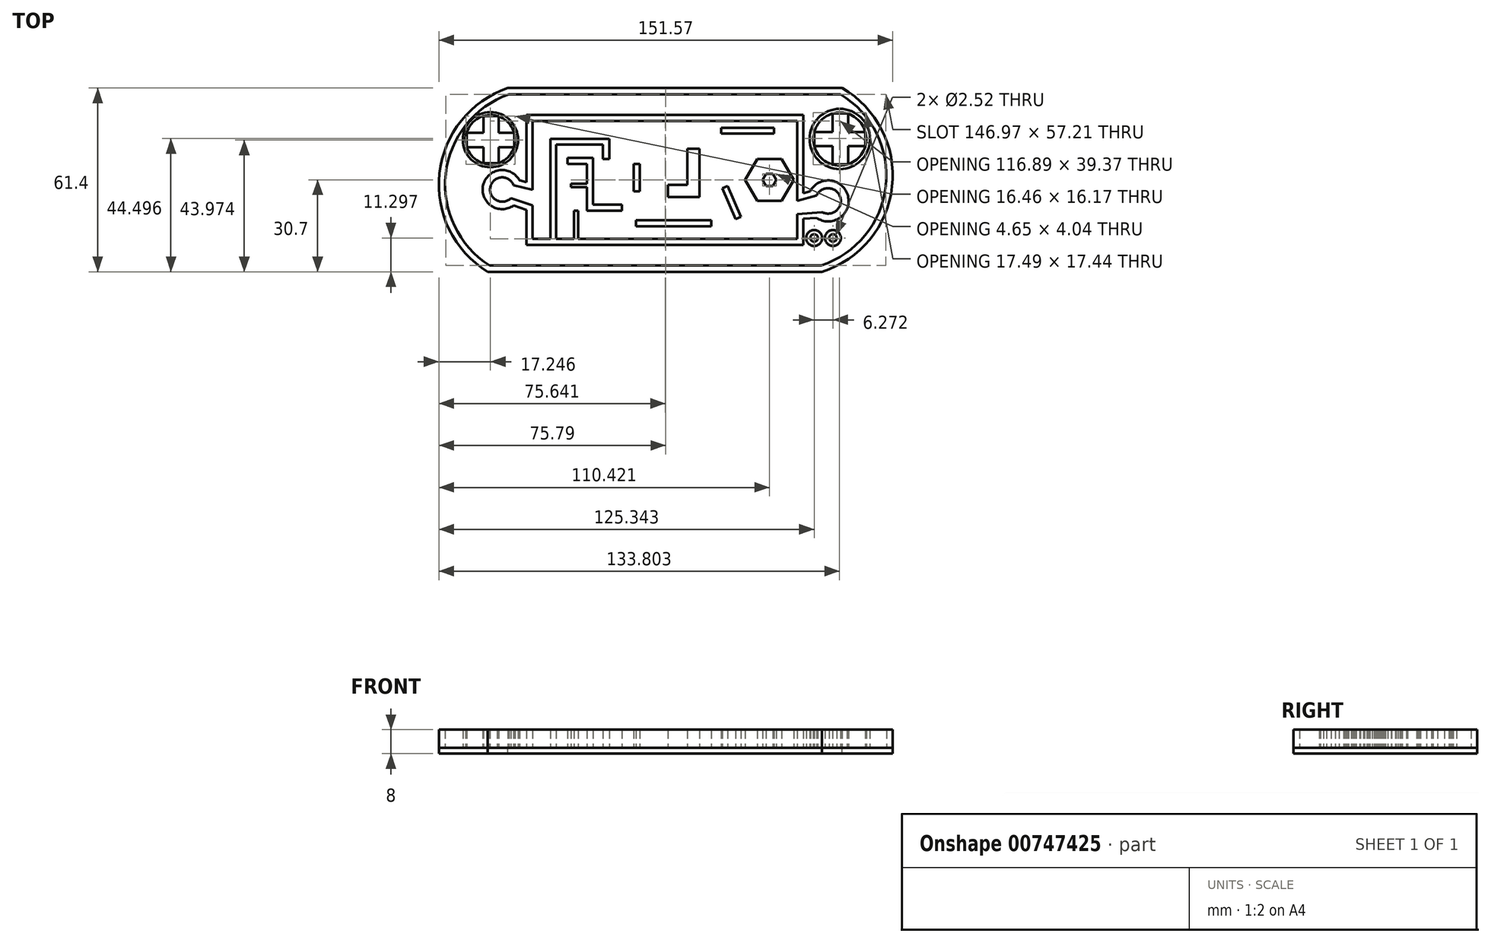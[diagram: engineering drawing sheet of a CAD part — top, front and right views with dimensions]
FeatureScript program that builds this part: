
annotation { "Feature Type Name" : "Feature", "Feature Type Description" : "" }
export const myFeature = defineFeature(function(context is Context, id is Id, definition is map)
    precondition{}
    {
        {
            var Q0;
            Q0=qCreatedBy(makeId("Top.planeOp"),FACE);
            var sketch = newSketch(context, id + "F0", { "sketchPlane" : qUnion([Q0])});
            skLineSegment(sketch, "E0.bottom", {"start": v(-52.45, 30.7) * mm, "end": v(59.2, 30.7) * mm});
            skLineSegment(sketch, "E0.top", {"start": v(-59.2, -30.7) * mm, "end": v(52.45, -30.7) * mm});
            skPoint(sketch, "E0.middle", {"position": v(0, 0) * mm});
            skArc(sketch, "E1", {"start": v(-52.45, 30.7) * mm, "mid": v(-75.31, 2.14) * mm, "end": v(-59.2, -30.7) * mm});
            skArc(sketch, "E2", {"start": v(52.45, -30.7) * mm, "mid": v(75.85, -2.2) * mm, "end": v(59.2, 30.7) * mm});
            skLineSegment(sketch, "E3.bottom", {"start": v(-46.23, 21.68) * mm, "end": v(46.23, 21.68) * mm});
            skLineSegment(sketch, "E3.top", {"start": v(-46.23, -21.68) * mm, "end": v(46.23, -21.68) * mm});
            skLineSegment(sketch, "E3.left", {"start": v(-46.23, 21.68) * mm, "end": v(-46.23, -0.76) * mm});
            skLineSegment(sketch, "E3.right", {"start": v(46.23, 21.68) * mm, "end": v(46.23, -4.42) * mm});
            skCircle(sketch, "E4", {"center": v(-58.27, 13.42) * mm, "radius": 8.27 * mm});
            skLineSegment(sketch, "E5.bottom", {"start": v(-60.57, 21.36) * mm, "end": v(-55.57, 21.36) * mm});
            skLineSegment(sketch, "E5.top", {"start": v(-60.57, 5.6) * mm, "end": v(-55.57, 5.6) * mm});
            skLineSegment(sketch, "E5.left", {"start": v(-60.57, 21.36) * mm, "end": v(-60.57, 15.78) * mm});
            skLineSegment(sketch, "E5.right", {"start": v(-55.57, 21.36) * mm, "end": v(-55.57, 15.78) * mm});
            skLineSegment(sketch, "E6.bottom", {"start": v(-66.16, 10.93) * mm, "end": v(-60.57, 10.93) * mm});
            skLineSegment(sketch, "E6.top", {"start": v(-66.16, 15.78) * mm, "end": v(-60.57, 15.78) * mm});
            skLineSegment(sketch, "E6.left", {"start": v(-66.16, 10.93) * mm, "end": v(-66.16, 15.78) * mm});
            skLineSegment(sketch, "E6.right", {"start": v(-50.36, 10.93) * mm, "end": v(-50.36, 15.78) * mm});
            skLineSegment(sketch, "E7", {"start": v(-55.57, 15.78) * mm, "end": v(-58.27, 13.42) * mm});
            skLineSegment(sketch, "E8", {"start": v(-55.57, 10.93) * mm, "end": v(-58.27, 13.42) * mm});
            skLineSegment(sketch, "E9", {"start": v(-58.27, 13.42) * mm, "end": v(-60.57, 10.93) * mm});
            skLineSegment(sketch, "E10", {"start": v(-58.27, 13.42) * mm, "end": v(-60.57, 15.78) * mm});
            skLineSegment(sketch, "E11.trimOffspring", {"start": v(-55.57, 10.93) * mm, "end": v(-55.57, 5.6) * mm});
            skLineSegment(sketch, "E12.trimOffspring", {"start": v(-55.57, 15.78) * mm, "end": v(-50.36, 15.78) * mm});
            skLineSegment(sketch, "E13.trimOffspring", {"start": v(-60.57, 10.93) * mm, "end": v(-60.57, 5.6) * mm});
            skLineSegment(sketch, "E14.trimOffspring", {"start": v(-55.57, 10.93) * mm, "end": v(-50.36, 10.93) * mm});
            skArc(sketch, "E15", {"start": v(-48.56, -0.18) * mm, "mid": v(-60.71, -1.71) * mm, "end": v(-50.56, -8.57) * mm});
            skPoint(sketch, "E16.start.orphan", {"position": v(-60.98, 5.6) * mm});
            skArc(sketch, "E17", {"start": v(-50.57, -1.75) * mm, "mid": v(-58.32, -2.38) * mm, "end": v(-51.51, -6.14) * mm});
            skCircle(sketch, "E18", {"center": v(58.4, 13.66) * mm, "radius": 8.85 * mm});
            skArc(sketch, "E19", {"start": v(50.6, -12.67) * mm, "mid": v(61.14, -5.42) * mm, "end": v(48.46, -3.79) * mm});
            skArc(sketch, "E20", {"start": v(52.48, -10.76) * mm, "mid": v(58.52, -5.71) * mm, "end": v(50.67, -5.19) * mm});
            skCircle(sketch, "E21", {"center": v(49.82, -19.4) * mm, "radius": 2.66 * mm});
            skCircle(sketch, "E22", {"center": v(56.1, -19.4) * mm, "radius": 2.66 * mm});
            skCircle(sketch, "E23", {"center": v(49.82, -19.4) * mm, "radius": 1.26 * mm});
            skCircle(sketch, "E24", {"center": v(56.1, -19.4) * mm, "radius": 1.26 * mm});
            skLineSegment(sketch, "E25.0", {"start": v(-44.23, 19.68) * mm, "end": v(44.23, 19.68) * mm});
            skLineSegment(sketch, "E25.1", {"start": v(-44.23, 19.68) * mm, "end": v(-44.23, -3.32) * mm});
            skLineSegment(sketch, "E25.2", {"start": v(-44.23, -19.68) * mm, "end": v(44.23, -19.68) * mm});
            skLineSegment(sketch, "E25.3", {"start": v(44.23, 19.68) * mm, "end": v(44.23, -7.03) * mm});
            skArc(sketch, "E26.0", {"start": v(-52.1, 28.6) * mm, "mid": v(-73.22, 2.03) * mm, "end": v(-58.6, -28.6) * mm});
            skLineSegment(sketch, "E26.1", {"start": v(-52.1, 28.6) * mm, "end": v(58.63, 28.6) * mm});
            skArc(sketch, "E26.2", {"start": v(52.12, -28.6) * mm, "mid": v(73.76, -2.1) * mm, "end": v(58.63, 28.6) * mm});
            skLineSegment(sketch, "E26.3", {"start": v(-58.6, -28.6) * mm, "end": v(52.12, -28.6) * mm});
            skCircle(sketch, "E27.0", {"center": v(-58.27, 13.42) * mm, "radius": 9.22 * mm});
            skLineSegment(sketch, "E28.bottom", {"start": v(56.04, 22.2) * mm, "end": v(61.19, 22.2) * mm});
            skLineSegment(sketch, "E28.top", {"start": v(56.04, 5.26) * mm, "end": v(61.19, 5.26) * mm});
            skLineSegment(sketch, "E28.left", {"start": v(56.04, 22.2) * mm, "end": v(56.04, 15.97) * mm});
            skLineSegment(sketch, "E28.right", {"start": v(61.19, 22.2) * mm, "end": v(61.19, 15.97) * mm});
            skLineSegment(sketch, "E29.bottom", {"start": v(49.84, 15.97) * mm, "end": v(56.04, 15.97) * mm});
            skLineSegment(sketch, "E29.top", {"start": v(49.84, 11.24) * mm, "end": v(56.04, 11.24) * mm});
            skLineSegment(sketch, "E29.left", {"start": v(49.84, 15.97) * mm, "end": v(49.84, 11.24) * mm});
            skLineSegment(sketch, "E29.right", {"start": v(66.9, 15.97) * mm, "end": v(66.9, 11.24) * mm});
            skLineSegment(sketch, "E30", {"start": v(56.04, 11.24) * mm, "end": v(61.19, 15.97) * mm});
            skLineSegment(sketch, "E31", {"start": v(56.04, 15.97) * mm, "end": v(61.19, 11.24) * mm});
            skLineSegment(sketch, "E32.trimOffspring", {"start": v(56.04, 11.24) * mm, "end": v(56.04, 5.26) * mm});
            skLineSegment(sketch, "E33.trimOffspring", {"start": v(61.19, 11.24) * mm, "end": v(66.9, 11.24) * mm});
            skLineSegment(sketch, "E34.trimOffspring", {"start": v(61.19, 15.97) * mm, "end": v(66.9, 15.97) * mm});
            skLineSegment(sketch, "E35.trimOffspring", {"start": v(61.19, 11.24) * mm, "end": v(61.19, 5.26) * mm});
            skCircle(sketch, "E36.0", {"center": v(58.4, 13.66) * mm, "radius": 10.08 * mm});
            skLineSegment(sketch, "E37", {"start": v(-38.3, -19.68) * mm, "end": v(-38.3, 13.77) * mm});
            skLineSegment(sketch, "E38", {"start": v(-38.3, 13.77) * mm, "end": v(-20.75, 13.77) * mm});
            skLineSegment(sketch, "E39.0", {"start": v(-36.3, 11.77) * mm, "end": v(-20.75, 11.77) * mm});
            skLineSegment(sketch, "E39.1", {"start": v(-36.3, -19.67) * mm, "end": v(-36.3, 11.77) * mm});
            skLineSegment(sketch, "E40", {"start": v(-20.75, 11.77) * mm, "end": v(-20.75, 7.03) * mm});
            skLineSegment(sketch, "E41", {"start": v(-20.75, 13.77) * mm, "end": v(-18.57, 13.77) * mm});
            skLineSegment(sketch, "E42", {"start": v(-18.57, 7.03) * mm, "end": v(-18.57, 13.77) * mm});
            skLineSegment(sketch, "E43", {"start": v(-32.6, 7.37) * mm, "end": v(-24, 7.37) * mm});
            skLineSegment(sketch, "E44", {"start": v(-24, 7.37) * mm, "end": v(-24, -8.32) * mm});
            skLineSegment(sketch, "E45", {"start": v(-24, -8.32) * mm, "end": v(-14.32, -8.32) * mm});
            skLineSegment(sketch, "E46.0", {"start": v(-26, -10.32) * mm, "end": v(-14.32, -10.32) * mm});
            skLineSegment(sketch, "E46.1", {"start": v(-26, 5.37) * mm, "end": v(-26, -1.23) * mm});
            skLineSegment(sketch, "E46.2", {"start": v(-32.6, 5.37) * mm, "end": v(-26, 5.37) * mm});
            skLineSegment(sketch, "E47", {"start": v(-26, -1.23) * mm, "end": v(-31.36, -1.23) * mm});
            skLineSegment(sketch, "E48.0", {"start": v(-26, -2.43) * mm, "end": v(-31.36, -2.43) * mm});
            skLineSegment(sketch, "E49", {"start": v(-32.6, 7.37) * mm, "end": v(-32.6, 5.37) * mm});
            skLineSegment(sketch, "E50", {"start": v(-20.75, 7.03) * mm, "end": v(-18.57, 7.03) * mm});
            skLineSegment(sketch, "E51", {"start": v(-31.36, -1.23) * mm, "end": v(-31.36, -2.43) * mm});
            skLineSegment(sketch, "E52", {"start": v(-14.32, -8.32) * mm, "end": v(-14.32, -10.32) * mm});
            skLineSegment(sketch, "E53", {"start": v(-10.38, -3.81) * mm, "end": v(-10.38, 5.37) * mm});
            skLineSegment(sketch, "E54.0", {"start": v(-8.38, -3.81) * mm, "end": v(-8.38, 5.37) * mm});
            skLineSegment(sketch, "E55", {"start": v(-10.38, 5.37) * mm, "end": v(-8.38, 5.37) * mm});
            skLineSegment(sketch, "E56", {"start": v(-10.38, -3.81) * mm, "end": v(-8.38, -3.81) * mm});
            skLineSegment(sketch, "E57", {"start": v(-9.73, -13.45) * mm, "end": v(15.5, -13.45) * mm});
            skLineSegment(sketch, "E58.0", {"start": v(-9.73, -15.45) * mm, "end": v(15.5, -15.45) * mm});
            skLineSegment(sketch, "E59", {"start": v(15.5, -13.45) * mm, "end": v(15.5, -15.45) * mm});
            skLineSegment(sketch, "E60", {"start": v(-9.73, -13.45) * mm, "end": v(-9.73, -15.45) * mm});
            skLineSegment(sketch, "E61", {"start": v(11.48, 10.42) * mm, "end": v(11.48, -5.68) * mm});
            skLineSegment(sketch, "E62", {"start": v(11.48, -5.68) * mm, "end": v(1.05, -5.68) * mm});
            skLineSegment(sketch, "E63", {"start": v(1.05, -5.68) * mm, "end": v(1.05, -1.68) * mm});
            skPoint(sketch, "E63.endSnap0", {"position": v(0, -1.68) * mm});
            skLineSegment(sketch, "E64", {"start": v(1.05, -1.68) * mm, "end": v(7.48, -1.68) * mm});
            skLineSegment(sketch, "E65", {"start": v(7.48, -1.68) * mm, "end": v(7.48, 10.39) * mm});
            skLineSegment(sketch, "E66", {"start": v(11.48, 10.42) * mm, "end": v(7.48, 10.42) * mm});
            skLineSegment(sketch, "E67", {"start": v(-30.4, -10.34) * mm, "end": v(-30.4, -19.68) * mm});
            skLineSegment(sketch, "E68.0", {"start": v(-28.93, -10.34) * mm, "end": v(-28.93, -19.67) * mm});
            skLineSegment(sketch, "E69", {"start": v(-30.4, -10.34) * mm, "end": v(-28.93, -10.34) * mm});
            skLineSegment(sketch, "E70", {"start": v(18.76, 15.44) * mm, "end": v(36.37, 15.44) * mm});
            skLineSegment(sketch, "E71.0", {"start": v(18.76, 17.44) * mm, "end": v(36.37, 17.44) * mm});
            skLineSegment(sketch, "E72", {"start": v(18.76, 17.44) * mm, "end": v(18.76, 15.44) * mm});
            skLineSegment(sketch, "E73", {"start": v(36.37, 17.44) * mm, "end": v(36.37, 15.44) * mm});
            skLineSegment(sketch, "E74.0", {"start": v(38.98, 7) * mm, "end": v(43, -0.04) * mm});
            skLineSegment(sketch, "E74.1", {"start": v(43, -0.04) * mm, "end": v(38.92, -7.03) * mm});
            skLineSegment(sketch, "E74.2", {"start": v(38.92, -7.03) * mm, "end": v(30.82, -7) * mm});
            skLineSegment(sketch, "E74.3", {"start": v(30.82, -7) * mm, "end": v(26.8, 0.04) * mm});
            skLineSegment(sketch, "E74.4", {"start": v(26.8, 0.04) * mm, "end": v(30.89, 7.03) * mm});
            skLineSegment(sketch, "E74.5", {"start": v(30.89, 7.03) * mm, "end": v(38.98, 7) * mm});
            skLineSegment(sketch, "E75.0", {"start": v(32.58, 0.01) * mm, "end": v(33.75, 2.02) * mm});
            skLineSegment(sketch, "E75.1", {"start": v(36.07, 2) * mm, "end": v(37.23, -0.01) * mm});
            skLineSegment(sketch, "E75.2", {"start": v(37.23, -0.01) * mm, "end": v(36.05, -2.02) * mm});
            skLineSegment(sketch, "E75.3", {"start": v(33.75, 2.02) * mm, "end": v(36.07, 2) * mm});
            skLineSegment(sketch, "E75.4", {"start": v(36.05, -2.02) * mm, "end": v(33.73, -2) * mm});
            skLineSegment(sketch, "E75.5", {"start": v(33.73, -2) * mm, "end": v(32.58, 0.01) * mm});
            skLineSegment(sketch, "E76", {"start": v(-50.57, -1.75) * mm, "end": v(-44.23, -3.32) * mm});
            skLineSegment(sketch, "E77", {"start": v(-51.51, -6.14) * mm, "end": v(-44.23, -8.58) * mm});
            skLineSegment(sketch, "E78.trimOffspring", {"start": v(-46.23, -10.02) * mm, "end": v(-46.23, -21.68) * mm});
            skLineSegment(sketch, "E79.0", {"start": v(-48.56, -0.18) * mm, "end": v(-46.23, -0.76) * mm});
            skLineSegment(sketch, "E80.0", {"start": v(-50.56, -8.57) * mm, "end": v(-46.23, -10.02) * mm});
            skLineSegment(sketch, "E81.trimOffspring", {"start": v(-44.23, -8.58) * mm, "end": v(-44.23, -19.68) * mm});
            skLineSegment(sketch, "E82.trimOffspring", {"start": v(46.23, -13.01) * mm, "end": v(46.23, -21.68) * mm});
            skLineSegment(sketch, "E83.trimOffspring", {"start": v(44.23, -11.41) * mm, "end": v(44.23, -19.68) * mm});
            skLineSegment(sketch, "E84", {"start": v(50.67, -5.19) * mm, "end": v(44.23, -7.03) * mm});
            skLineSegment(sketch, "E85", {"start": v(52.48, -10.76) * mm, "end": v(44.23, -11.41) * mm});
            skLineSegment(sketch, "E86.0", {"start": v(50.6, -12.67) * mm, "end": v(46.23, -13.01) * mm});
            skLineSegment(sketch, "E87.0", {"start": v(48.46, -3.79) * mm, "end": v(46.23, -4.42) * mm});
            skLineSegment(sketch, "E88", {"start": v(19.09, -2.79) * mm, "end": v(23.55, -13.1) * mm});
            skLineSegment(sketch, "E89.0", {"start": v(20.92, -2) * mm, "end": v(25.38, -12.3) * mm});
            skLineSegment(sketch, "E90", {"start": v(19.09, -2.79) * mm, "end": v(20.92, -2) * mm});
            skLineSegment(sketch, "E91", {"start": v(23.55, -13.1) * mm, "end": v(25.38, -12.3) * mm});
            skLineSegment(sketch, "E92.trimOffspring", {"start": v(-26, -2.43) * mm, "end": v(-26, -10.32) * mm});
            skLineSegment(sketch, "E93", {"start": v(-36.3, -19.67) * mm, "end": v(-36.3, -19.68) * mm});
            skLineSegment(sketch, "E94", {"start": v(-28.93, -19.67) * mm, "end": v(-28.93, -19.68) * mm});
            skLineSegment(sketch, "E95", {"start": v(7.48, 10.42) * mm, "end": v(7.48, 10.39) * mm});
            skSolve(sketch);
        }
        {
            var Q0;
            Q0 = qSketchRegion(id + "F0", true);
            var Q1;
            Q1=makeQuery(id+"F0.imprint","IMPRINT",FACE,{"disambiguationData":[TD([[makeQuery(id+"F0.imprint","IMPRINT",EDGE,{"derivedFrom":sQuery(id+"F0.wireOp",EDGE,"E27.0")}),1.0]])]});
            var Q2;
            {var subQ4=sQuery(id+"F0.wireOp",EDGE,"E5.left");Q2=makeQuery(id+"F0.imprint","IMPRINT",FACE,{"disambiguationData":[TD([[makeQuery(id+"F0.imprint","IMPRINT",EDGE,{"derivedFrom":subQ4}),1.0]])]});}
            var Q3;
            Q3=makeQuery(id+"F0.imprint","IMPRINT",FACE,{"disambiguationData":[TD([[makeQuery(id+"F0.imprint","IMPRINT",EDGE,{"derivedFrom":sQuery(id+"F0.wireOp",EDGE,"E5.top")}),1.0]])]});
            var Q4;
            Q4=makeQuery(id+"F0.imprint","IMPRINT",FACE,{"disambiguationData":[TD([[makeQuery(id+"F0.imprint","IMPRINT",EDGE,{"derivedFrom":sQuery(id+"F0.wireOp",EDGE,"E6.bottom")}),1.0]])]});
            var Q5;
            Q5=makeQuery(id+"F0.imprint","IMPRINT",FACE,{"disambiguationData":[TD([[makeQuery(id+"F0.imprint","IMPRINT",EDGE,{"derivedFrom":sQuery(id+"F0.wireOp",EDGE,"E7")}),1.0]])]});
            var Q6;
            Q6=makeQuery(id+"F0.imprint","IMPRINT",FACE,{"disambiguationData":[TD([[makeQuery(id+"F0.imprint","IMPRINT",EDGE,{"derivedFrom":sQuery(id+"F0.wireOp",EDGE,"E3.bottom")}),-1.0]])]});
            var Q7;
            Q7=makeQuery(id+"F0.imprint","IMPRINT",FACE,{"disambiguationData":[TD([[makeQuery(id+"F0.imprint","IMPRINT",EDGE,{"derivedFrom":sQuery(id+"F0.wireOp",EDGE,"E43")}),-1.0]])]});
            var Q8;
            Q8=makeQuery(id+"F0.imprint","IMPRINT",FACE,{"disambiguationData":[TD([[makeQuery(id+"F0.imprint","IMPRINT",EDGE,{"derivedFrom":sQuery(id+"F0.wireOp",EDGE,"E74.0")}),-1.0]])]});
            var Q9;
            Q9=makeQuery(id+"F0.imprint","IMPRINT",FACE,{"disambiguationData":[TD([[makeQuery(id+"F0.imprint","IMPRINT",EDGE,{"derivedFrom":sQuery(id+"F0.wireOp",EDGE,"E53")}),-1.0]])]});
            var Q10;
            Q10=makeQuery(id+"F0.imprint","IMPRINT",FACE,{"disambiguationData":[TD([[makeQuery(id+"F0.imprint","IMPRINT",EDGE,{"derivedFrom":sQuery(id+"F0.wireOp",EDGE,"E57")}),-1.0]])]});
            var Q11;
            Q11=makeQuery(id+"F0.imprint","IMPRINT",FACE,{"disambiguationData":[TD([[makeQuery(id+"F0.imprint","IMPRINT",EDGE,{"derivedFrom":sQuery(id+"F0.wireOp",EDGE,"E88")}),1.0]])]});
            var Q12;
            Q12=makeQuery(id+"F0.imprint","IMPRINT",FACE,{"disambiguationData":[TD([[makeQuery(id+"F0.imprint","IMPRINT",EDGE,{"derivedFrom":sQuery(id+"F0.wireOp",EDGE,"E70")}),1.0]])]});
            var Q13;
            Q13=makeQuery(id+"F0.imprint","IMPRINT",FACE,{"disambiguationData":[TD([[makeQuery(id+"F0.imprint","IMPRINT",EDGE,{"derivedFrom":sQuery(id+"F0.wireOp",EDGE,"E36.0")}),1.0]])]});
            var Q14;
            {var subQ0=sQuery(id+"F0.wireOp",EDGE,"E28.left");Q14=makeQuery(id+"F0.imprint","IMPRINT",FACE,{"disambiguationData":[TD([[makeQuery(id+"F0.imprint","IMPRINT",EDGE,{"derivedFrom":subQ0}),1.0]])]});}
            var Q15;
            Q15=makeQuery(id+"F0.imprint","IMPRINT",FACE,{"disambiguationData":[TD([[makeQuery(id+"F0.imprint","IMPRINT",EDGE,{"derivedFrom":sQuery(id+"F0.wireOp",EDGE,"E29.right")}),-1.0]])]});
            var Q16;
            {var subQ5=sQuery(id+"F0.wireOp",EDGE,"E29.bottom");Q16=makeQuery(id+"F0.imprint","IMPRINT",FACE,{"disambiguationData":[TD([[makeQuery(id+"F0.imprint","IMPRINT",EDGE,{"derivedFrom":subQ5}),-1.0]])]});}
            var Q17;
            Q17=makeQuery(id+"F0.imprint","IMPRINT",FACE,{"disambiguationData":[TD([[makeQuery(id+"F0.imprint","IMPRINT",EDGE,{"derivedFrom":sQuery(id+"F0.wireOp",EDGE,"E28.top")}),1.0]])]});
            var Q18;
            Q18=makeQuery(id+"F0.imprint","IMPRINT",FACE,{"disambiguationData":[TD([[makeQuery(id+"F0.imprint","IMPRINT",EDGE,{"derivedFrom":sQuery(id+"F0.wireOp",EDGE,"E21")}),1.0]])]});
            var Q19;
            Q19=makeQuery(id+"F0.imprint","IMPRINT",FACE,{"disambiguationData":[TD([[makeQuery(id+"F0.imprint","IMPRINT",EDGE,{"derivedFrom":sQuery(id+"F0.wireOp",EDGE,"E22")}),1.0]])]});
            var Q20;
            {var subQ0=sQuery(id+"F0.wireOp",EDGE,"E37");Q20=makeQuery(id+"F0.imprint","IMPRINT",FACE,{"disambiguationData":[TD([[makeQuery(id+"F0.imprint","IMPRINT",EDGE,{"derivedFrom":subQ0}),-1.0]])]});}
            var Q21;
            {var subQ0=sQuery(id+"F0.wireOp",EDGE,"E67");Q21=makeQuery(id+"F0.imprint","IMPRINT",FACE,{"disambiguationData":[TD([[makeQuery(id+"F0.imprint","IMPRINT",EDGE,{"derivedFrom":subQ0}),1.0]])]});}
            var Q22;
            Q22=makeQuery(id+"F0.imprint","IMPRINT",FACE,{"disambiguationData":[TD([[makeQuery(id+"F0.imprint","IMPRINT",EDGE,{"derivedFrom":sQuery(id+"F0.wireOp",EDGE,"E61")}),-1.0]])]});
            extrude(context, id + "F1", {"entities" : qUnion([Q0, Q1, Q2, Q3, Q4, Q5, Q6, Q7, Q8, Q9, Q10, Q11, Q12, Q13, Q14, Q15, Q16, Q17, Q18, Q19, Q20, Q21, Q22]), "depth" : 6 * mm, "offsetDistance" : 25 * mm});
        }
        {
            var Q0;
            Q0=qCreatedBy(makeId("Top.planeOp"),FACE);
            var sketch = newSketch(context, id + "F2", { "sketchPlane" : qUnion([Q0])});
            skLineSegment(sketch, "E96.0", {"start": v(-59.2, -30.7) * mm, "end": v(52.45, -30.7) * mm});
            skArc(sketch, "E97.0", {"start": v(52.45, -30.7) * mm, "mid": v(75.85, -2.2) * mm, "end": v(59.2, 30.7) * mm});
            skLineSegment(sketch, "E98.0", {"start": v(-52.45, 30.7) * mm, "end": v(59.2, 30.7) * mm});
            skArc(sketch, "E99.0", {"start": v(-52.45, 30.7) * mm, "mid": v(-75.31, 2.14) * mm, "end": v(-59.2, -30.7) * mm});
            skSolve(sketch);
        }
        {
            var Q0;
            Q0 = qSketchRegion(id + "F2", true);
            extrude(context, id + "F3", {"entities" : qUnion([Q0]), "oppositeDirection" : true, "depth" : 2 * mm, "offsetDistance" : 25 * mm});
        }
    });
